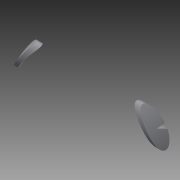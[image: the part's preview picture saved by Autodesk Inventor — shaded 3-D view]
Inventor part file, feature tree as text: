
AUTODESK INVENTOR PART (.ipt)
format: ipt  version: 2015 (Build 190159000, 159)  size: 107,008 bytes
history: native  units: in
note: dims shown in document units (in); Inventor stores cm internally (conversion verified against a paired STEP export)
features: sketch x2, extrude x1, revolve x1
ambient origin geometry x8: Origin, YZ Plane, XZ Plane, XY Plane, X Axis, Y Axis, Z Axis, Center Point
bodies: Solid1 (feature_tree)
feature tree (4):
  extrude  "Extrusion1"  Depth=0.3in
  revolve  "Revolution1"  Angle=15.0deg
  sketch  "Sketch1"  dims[d0=0.15in d1=0.3in]
  sketch  "Sketch2"  dims[d2=0.175in d3=15.0deg d4=15.0deg d5=2.0in d6=0.0in d7=0.04in d8=90.0deg]
